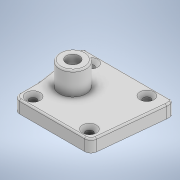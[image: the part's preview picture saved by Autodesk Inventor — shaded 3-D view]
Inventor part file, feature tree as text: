
AUTODESK INVENTOR PART (.ipt)
format: ipt  version: 2020.3 (Build 243373000, 373)  size: 223,232 bytes
history: native  units: mm
features: other x3, sketch x2
ambient origin geometry x8: Origin, YZ Plane, XZ Plane, XY Plane, X Axis, Y Axis, Z Axis, Center Point
bodies: Solid1 (feature_tree)
feature tree (5):
  other  "LegPin_Side_v1.ipt"
  other  "Solid6::LegPin_Side_v1.ipt"
  other  "TaggingFeature1"
  sketch  "Sketch1"  dims[d0=10.0mm]
  sketch  "Sketch2"
